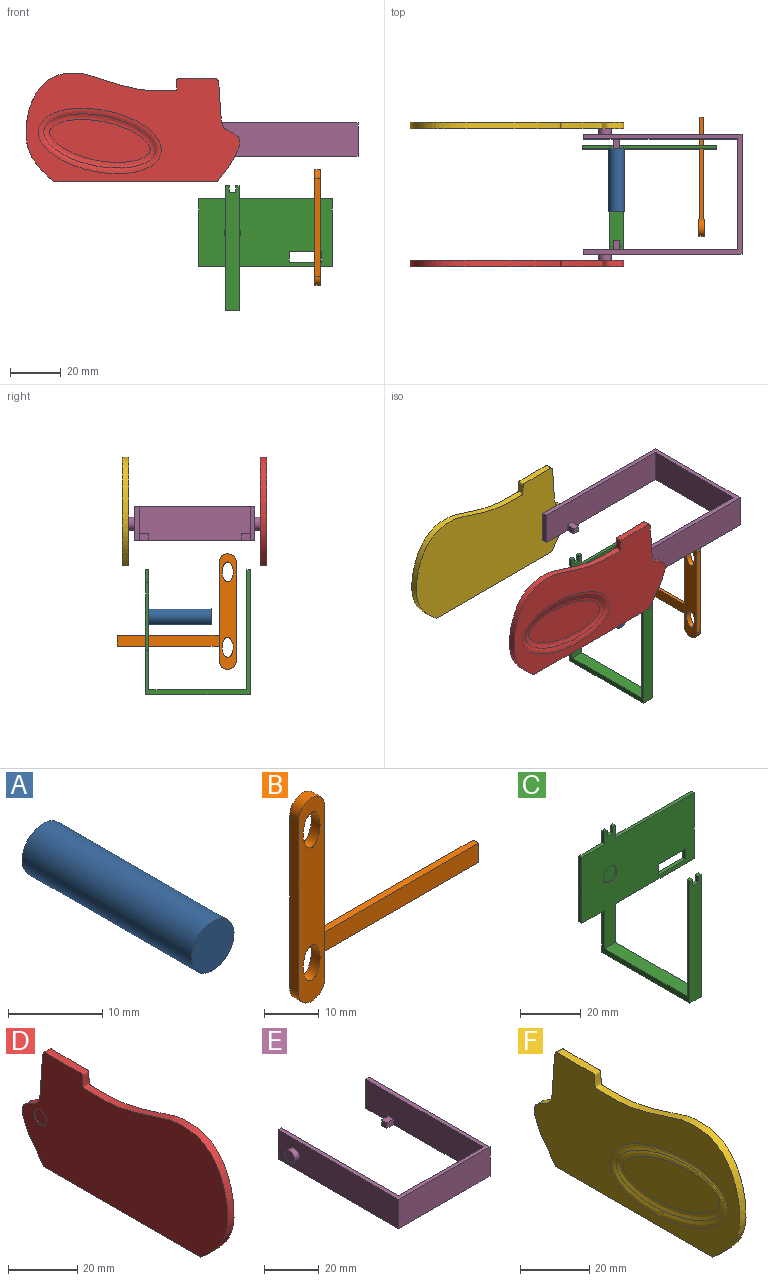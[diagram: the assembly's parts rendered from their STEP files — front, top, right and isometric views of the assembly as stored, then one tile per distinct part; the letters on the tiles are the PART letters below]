
ASSEMBLY  parts=6 mates=5
PART A: 3 faces, bbox 6.4x25.4x6.4 mm
  f0: cylinder r=3.17mm len=25.4mm, axis (0,-1,0), area 506.7mm2, adj f1,f2
  f1: plane 6.35x6.35mm, normal (0,1,0), area 31.7mm2, adj f0
  f2: plane 6.35x6.35mm, normal (0,-1,0), area 31.7mm2, adj f0
PART B: 13 faces, bbox 46.9x2.3x45.5 mm
  f0: plane 38.69x2.29mm, normal (1,0,0), area 82.5mm2, adj f1,f3,f4,f5,f8,f9,f10,f11
  f1: cylinder r=3.39mm len=6.79mm, axis (0,1,0), area 24.4mm2, adj f0,f2,f4,f5
  f2: plane 38.69x2.29mm, normal (-1,0,0), area 88.4mm2, adj f1,f3,f4,f5
  f3: cylinder r=3.39mm len=6.79mm, axis (0,1,0), area 24.4mm2, adj f0,f2,f4,f5
  f4: plane 45.48x6.79mm, normal (0,-1,0), area 245.5mm2, adj f0,f1,f2,f3,f6,f7
  f5: plane 45.48x6.79mm, normal (0,1,0), area 245.5mm2, adj f0,f1,f2,f3,f6,f7
  f6: extruded ~7.84x4.34mm, area 44.6mm2, adj f4,f5
  f7: extruded ~7.84x4.34mm, area 44.6mm2, adj f4,f5
  f8: plane 40.13x4.29mm, normal (0,-1,0), area 172.3mm2, adj f0,f9,f11,f12
  f9: plane 40.13x1.38mm, normal (0,0,-1), area 55.3mm2, adj f0,f8,f10,f12
  f10: plane 40.13x4.29mm, normal (0,1,0), area 172.3mm2, adj f0,f9,f11,f12
  f11: plane 40.13x1.38mm, normal (0,0,1), area 55.3mm2, adj f0,f8,f10,f12
  f12: plane 4.29x1.38mm, normal (1,0,0), area 5.9mm2, adj f8,f9,f10,f11
PART C: 32 faces, bbox 52.6x41.1x49.3 mm
  f0: plane 52.56x47.29mm, normal (0,-1,0), area 1411.2mm2, adj f3,f4,f5,f6,f7,f8,f9,f10
  f1: plane 52.56x49.28mm, normal (0,1,0), area 1453.2mm2, adj f4,f5,f6,f7,f8,f9,f10,f11
  f2: plane 1.3x1.28mm, normal (0,0,1), area 1.7mm2, adj f12,f22,f23,f27
  f3: plane 38.58x5.19mm, normal (0,0,1), area 200.2mm2, adj f0,f12,f13,f23
  f4: plane 2.54x1.27mm, normal (-1,0,0), area 3.2mm2, adj f0,f1,f5,f18
  f5: plane 2.65x1.27mm, normal (0,0,1), area 3.4mm2, adj f0,f1,f4,f6
  f6: plane 2.54x1.27mm, normal (1,0,0), area 3.2mm2, adj f0,f1,f5,f7
  f7: plane 1.27x1.27mm, normal (0,0,1), area 1.6mm2, adj f0,f1,f6,f8
  f8: plane 5.17x1.27mm, normal (-1,0,0), area 6.6mm2, adj f0,f1,f7,f9
  f9: plane 10.65x1.27mm, normal (0,0,1), area 13.5mm2, adj f0,f1,f8,f10
  f10: plane 26.57x1.27mm, normal (-1,0,0), area 33.7mm2, adj f0,f1,f9,f11
  f11: plane 10.65x1.27mm, normal (0,0,-1), area 13.5mm2, adj f0,f1,f10,f12
  f12: plane 49.28x41.15mm, normal (-1,0,0), area 163.2mm2, adj f0,f1,f2,f3,f11,f21,f22,f23
  f13: plane 49.28x41.15mm, normal (1,0,0), area 163.2mm2, adj f0,f1,f3,f14,f21,f22,f23,f24
  f14: plane 36.72x1.27mm, normal (0,0,-1), area 46.6mm2, adj f0,f1,f13,f15
  f15: plane 26.57x1.27mm, normal (1,0,0), area 33.7mm2, adj f0,f1,f14,f16
  f16: plane 36.72x1.27mm, normal (0,0,1), area 46.6mm2, adj f0,f1,f15,f17
  f17: plane 5.17x1.27mm, normal (1,0,0), area 6.6mm2, adj f0,f1,f16,f18
  f18: plane 1.27x1.27mm, normal (0,0,1), area 1.6mm2, adj f0,f1,f4,f17
  f19: cylinder r=3.17mm len=6.35mm, axis (0,-1,0), area 12.7mm2, adj f0,f20
  f20: plane 6.35x6.35mm, normal (0,-1,0), area 31.7mm2, adj f19
  f21: plane 41.15x5.19mm, normal (0,0,-1), area 213.5mm2, adj f1,f12,f13,f22
  f22: plane 49.28x5.19mm, normal (0,-1,0), area 249.1mm2, adj f2,f12,f13,f21,f24,f25,f26,f27
  f23: plane 47.29x5.19mm, normal (0,1,0), area 238.7mm2, adj f2,f3,f12,f13,f24,f25,f26,f27
  f24: plane 1.3x1.27mm, normal (0,0,1), area 1.7mm2, adj f13,f22,f23,f25
  f25: plane 2.54x1.3mm, normal (-1,0,0), area 3.3mm2, adj f22,f23,f24,f26
  f26: plane 2.64x1.3mm, normal (0,0,1), area 3.4mm2, adj f22,f23,f25,f27
  f27: plane 2.54x1.3mm, normal (1,0,0), area 3.3mm2, adj f2,f22,f23,f26
  f28: plane 12.7x1.27mm, normal (0,0,-1), area 16.1mm2, adj f0,f1,f29,f31
  f29: plane 4.3x1.27mm, normal (1,0,0), area 5.5mm2, adj f0,f1,f28,f30
  f30: plane 12.7x1.27mm, normal (0,0,1), area 16.1mm2, adj f0,f1,f29,f31
  f31: plane 4.3x1.27mm, normal (-1,0,0), area 5.5mm2, adj f0,f1,f28,f30
PART D: 10 faces, bbox 2.5x85x43.3 mm
  f0: plane 8.26x6.04mm, normal (0,0.81,-0.59), area 26mm2, adj f1,f2,f3,f4
  f1: extruded ~84.12x42.8mm, area 406.9mm2, adj f0,f2,f3,f4
  f2: plane 64.32x2.54mm, normal (0,0,-1), area 163.4mm2, adj f0,f1,f3,f4
  f3: plane 84.95x43.31mm, normal (-1,0,0), area 2979.2mm2, adj f0,f1,f2,f5
  f4: plane 84.95x43.31mm, normal (1,0,0), area 2053.9mm2, adj f0,f1,f2,f9
  f5: cylinder r=2.54mm len=5.08mm, axis (-1,0,0), area 4.1mm2, adj f3,f6
  f6: plane 5.08x5.08mm, normal (-1,0,0), area 20.3mm2, adj f5
  f7: plane 39.64x16.93mm, normal (1,0,0), area 479.3mm2, adj f8
  f8: bspline ~43.8x21.36mm, area 225.7mm2, adj f7,f9
  f9: bspline ~48.51x25.79mm, area 256.5mm2, adj f4,f8
PART E: 22 faces, bbox 52.3x62.6x13.1 mm
  f0: plane 43.69x13.09mm, normal (0,1,0), area 572mm2, adj f1,f2,f4,f8
  f1: plane 60.82x13.09mm, normal (-1,0,0), area 789.6mm2, adj f0,f2,f3,f4,f14,f15,f16
  f2: plane 62.56x47.24mm, normal (0,0,-1), area 316.7mm2, adj f0,f1,f3,f5,f6,f7,f8,f9
  f3: plane 13.09x1.78mm, normal (0,1,0), area 23.3mm2, adj f1,f2,f4,f6
  f4: plane 62.56x47.24mm, normal (0,0,1), area 297.9mm2, adj f0,f1,f3,f5,f6,f7,f8,f9
  f5: plane 47.24x13.09mm, normal (0,-1,0), area 618.5mm2, adj f2,f4,f6,f7
  f6: plane 62.55x13.09mm, normal (1,0,0), area 798.7mm2, adj f2,f3,f4,f5,f20
  f7: plane 62.56x13.09mm, normal (-1,0,0), area 798.8mm2, adj f2,f4,f5,f9,f18
  f8: plane 60.83x13.09mm, normal (1,0,0), area 789.7mm2, adj f0,f2,f4,f9,f10,f11,f12
  f9: plane 13.09x1.78mm, normal (0,1,0), area 23.3mm2, adj f2,f4,f7,f8
  f10: plane 3.56x2.54mm, normal (0,1,0), area 9mm2, adj f2,f8,f11,f13
  f11: plane 3.56x2.64mm, normal (0,0,1), area 9.4mm2, adj f8,f10,f12,f13
  f12: plane 3.56x2.54mm, normal (0,-1,0), area 9mm2, adj f2,f8,f11,f13
  f13: plane 2.64x2.54mm, normal (1,0,0), area 6.7mm2, adj f2,f10,f11,f12
  f14: plane 3.56x2.54mm, normal (0,-1,0), area 9mm2, adj f1,f2,f15,f17
  f15: plane 3.56x2.64mm, normal (0,0,1), area 9.4mm2, adj f1,f14,f16,f17
  f16: plane 3.56x2.54mm, normal (0,1,0), area 9mm2, adj f1,f2,f15,f17
  f17: plane 2.64x2.54mm, normal (-1,0,0), area 6.7mm2, adj f2,f14,f15,f16
  f18: cylinder r=2.54mm len=5.08mm, axis (1,0,0), area 40.5mm2, adj f7,f19
  f19: plane 5.08x5.08mm, normal (-1,0,0), area 20.3mm2, adj f18
  f20: cylinder r=2.54mm len=5.08mm, axis (-1,0,0), area 40.5mm2, adj f6,f21
  f21: plane 5.08x5.08mm, normal (1,0,0), area 20.3mm2, adj f20
PART F: 10 faces, bbox 2.5x85x43.3 mm
  f0: plane 8.26x6.04mm, normal (0,0.81,-0.59), area 26mm2, adj f1,f2,f3,f4
  f1: extruded ~84.12x42.8mm, area 406.9mm2, adj f0,f2,f3,f4
  f2: plane 64.32x2.54mm, normal (0,0,-1), area 163.4mm2, adj f0,f1,f3,f4
  f3: plane 84.95x43.31mm, normal (-1,0,0), area 2057.1mm2, adj f0,f1,f2,f9
  f4: plane 84.95x43.31mm, normal (1,0,0), area 2979.2mm2, adj f0,f1,f2,f5
  f5: cylinder r=2.54mm len=5.08mm, axis (1,0,0), area 4.1mm2, adj f4,f6
  f6: plane 5.08x5.08mm, normal (1,0,0), area 20.3mm2, adj f5
  f7: plane 39.62x16.95mm, normal (-1,0,0), area 479.7mm2, adj f8
  f8: bspline ~45.72x23.05mm, area 226.1mm2, adj f7,f9
  f9: bspline ~48.5x25.81mm, area 256.5mm2, adj f3,f8
PLACE A rot(axis=(0.01,0.01,-1),0deg) t=(-11.31,-18.35,-11.86)mm
PLACE B rot(axis=(0,0,1),90deg) t=(21.09,-16.19,-32.68)mm
PLACE C rot(axis=(0.04,0.03,-1),0deg) t=(1.72,12.69,-11.86)mm
PLACE D rot(axis=(0,0,-1),90deg) t=(100.02,22.39,39.02)mm
PLACE E rot(axis=(0,0,1),90deg) t=(-24.42,17.06,18.24)mm
PLACE F rot(axis=(0,0,-1),90deg) t=(99.98,19.34,39.01)mm
MATE fastened D.f5 <-> E.f18  axis (0,1,0) through (-15.91,-32.73,24.78)mm
MATE fastened A.f0 <-> C.f19  axis (0,1,0) through (-11.31,12.06,-11.86)mm
MATE planar E.f14 <-> C.f4  axis (1,0,0) through (-9.99,13.5,19.51)mm
MATE planar C.f28 <-> B.f11  axis (0,0,-1) through (17.46,12.06,-19.2)mm
MATE fastened F.f5 <-> E.f20  axis (0,-1,0) through (-15.91,19.6,24.78)mm
